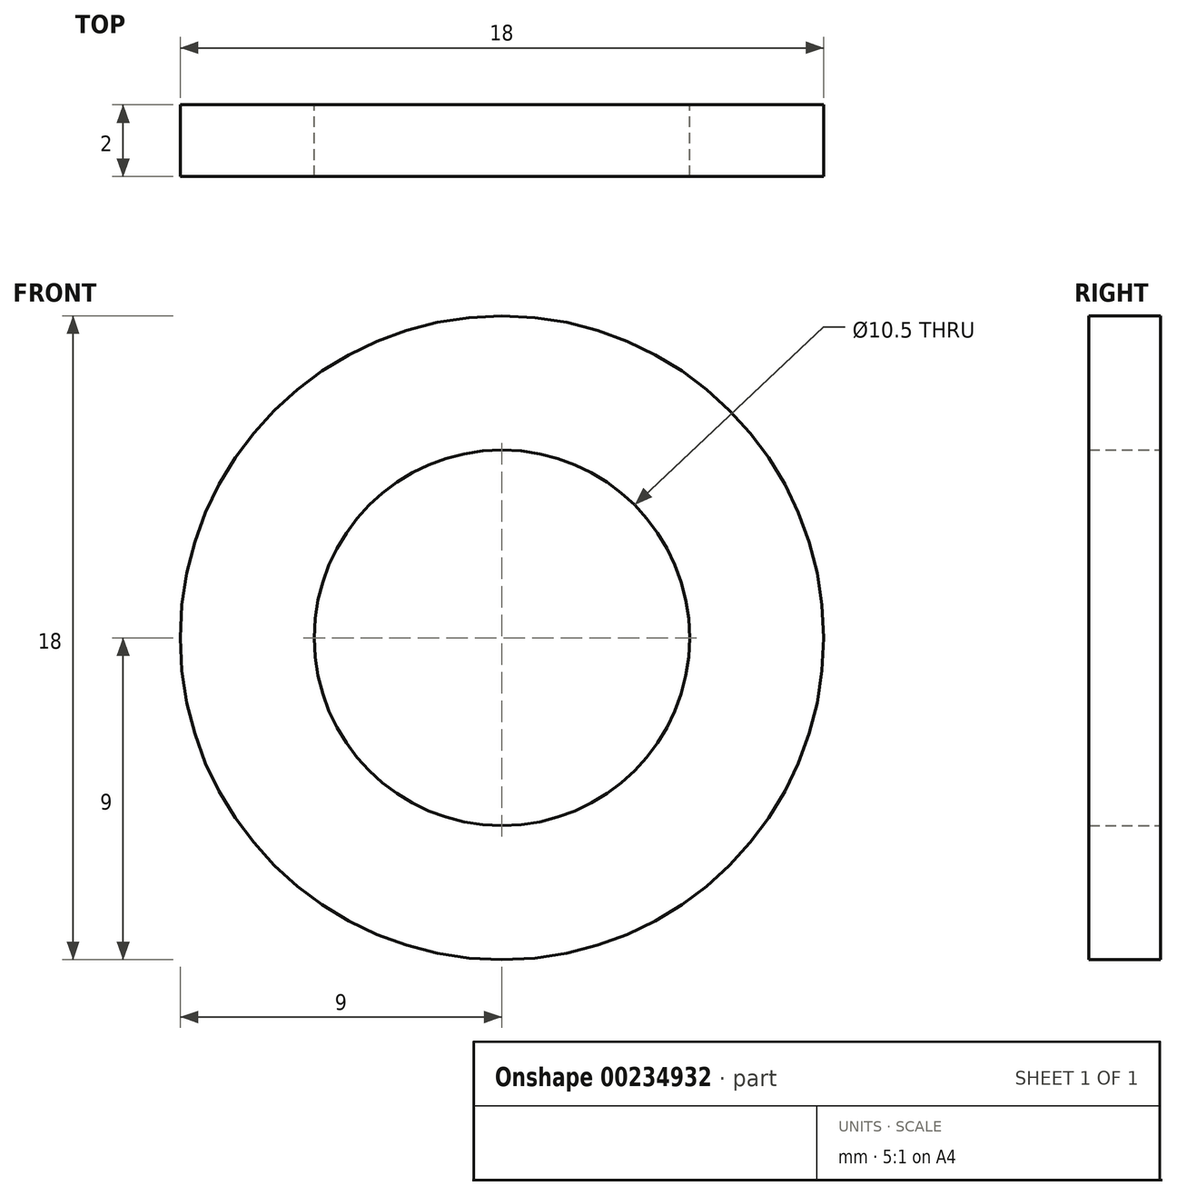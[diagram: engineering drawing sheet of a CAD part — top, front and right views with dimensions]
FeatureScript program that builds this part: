
annotation { "Feature Type Name" : "Feature", "Feature Type Description" : "" }
export const myFeature = defineFeature(function(context is Context, id is Id, definition is map)
    precondition{}
    {
        {
            var Q0;
            Q0=qCreatedBy(makeId("Front.planeOp"),FACE);
            var sketch = newSketch(context, id + "F0", { "sketchPlane" : qUnion([Q0])});
            skCircle(sketch, "E0", {"center": v(0, 0) * mm, "radius": 5.25 * mm});
            skCircle(sketch, "E1", {"center": v(0, 0) * mm, "radius": 9 * mm});
            skSolve(sketch);
        }
        {
            var Q0;
            Q0=makeQuery(id+"F0.imprint","IMPRINT",FACE,{"disambiguationData":[TD([[makeQuery(id+"F0.imprint","IMPRINT",EDGE,{"derivedFrom":sQuery(id+"F0.wireOp",EDGE,"E0")}),-1.0]])]});
            extrude(context, id + "F1", {"entities" : qUnion([Q0]), "endBound" : BoundingType.SYMMETRIC, "depth" : 2 * mm});
        }
    });
